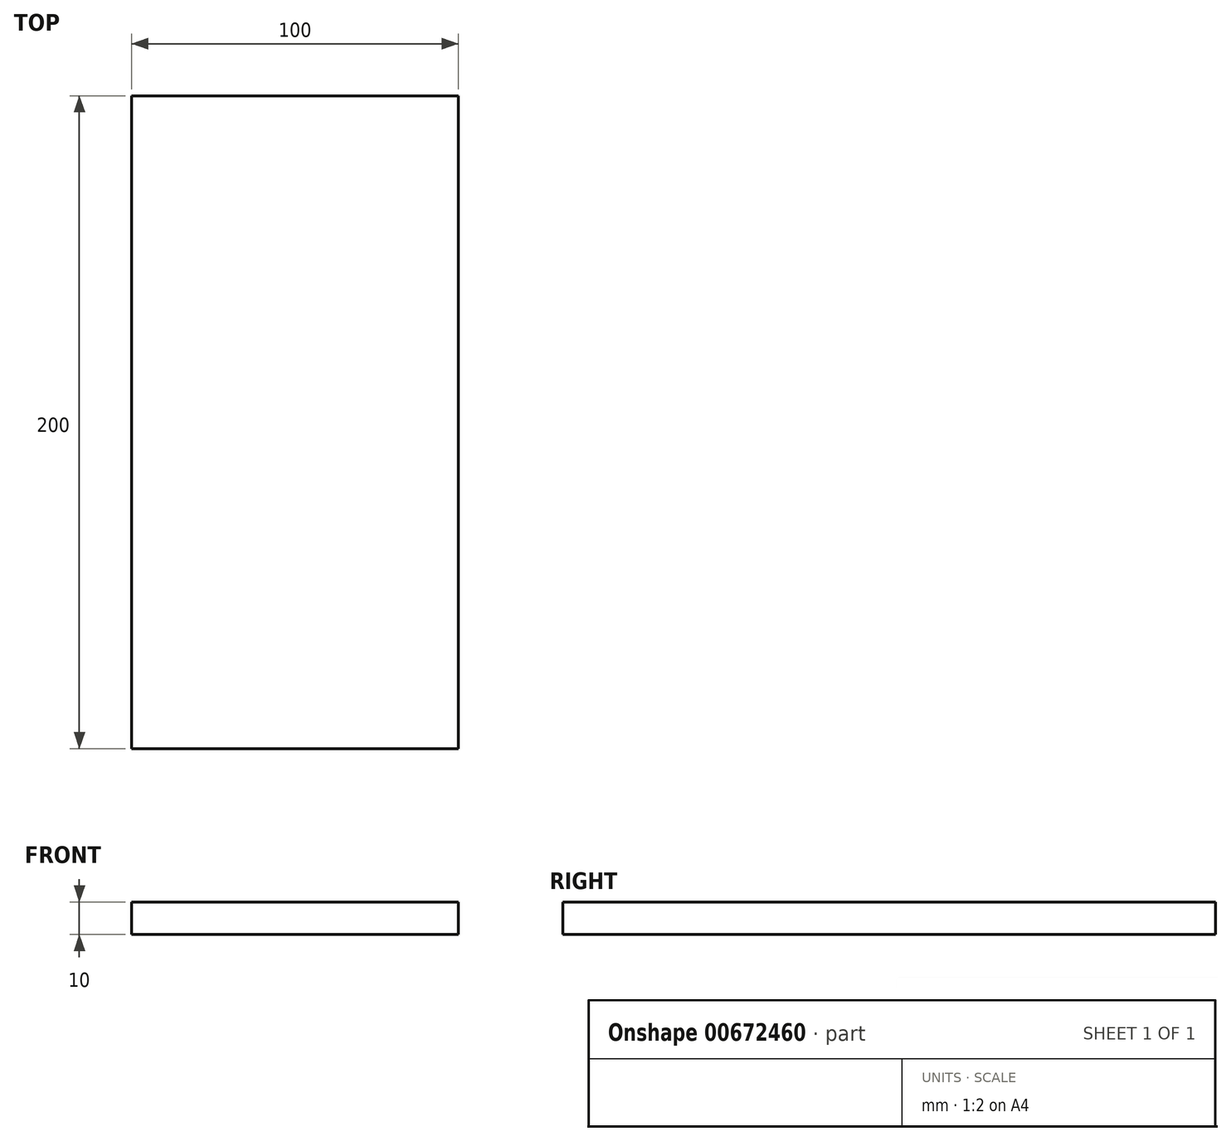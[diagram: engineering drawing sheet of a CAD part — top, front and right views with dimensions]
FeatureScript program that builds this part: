
annotation { "Feature Type Name" : "Feature", "Feature Type Description" : "" }
export const myFeature = defineFeature(function(context is Context, id is Id, definition is map)
    precondition{}
    {
        {
            var Q0;
            Q0=qCreatedBy(makeId("Top.planeOp"),FACE);
            var sketch = newSketch(context, id + "F0", { "sketchPlane" : qUnion([Q0])});
            skLineSegment(sketch, "E0.bottom", {"start": v(50, -100) * mm, "end": v(-50, -100) * mm});
            skLineSegment(sketch, "E0.top", {"start": v(50, 100) * mm, "end": v(-50, 100) * mm});
            skLineSegment(sketch, "E0.left", {"start": v(50, -100) * mm, "end": v(50, 100) * mm});
            skLineSegment(sketch, "E0.right", {"start": v(-50, -100) * mm, "end": v(-50, 100) * mm});
            skPoint(sketch, "E0.middle", {"position": v(0, 0) * mm});
            skSolve(sketch);
        }
        {
            var Q0;
            Q0 = qSketchRegion(id + "F0", true);
            extrude(context, id + "F1", {"entities" : qUnion([Q0]), "depth" : 10 * mm, "offsetDistance" : 25 * mm});
        }
    });
